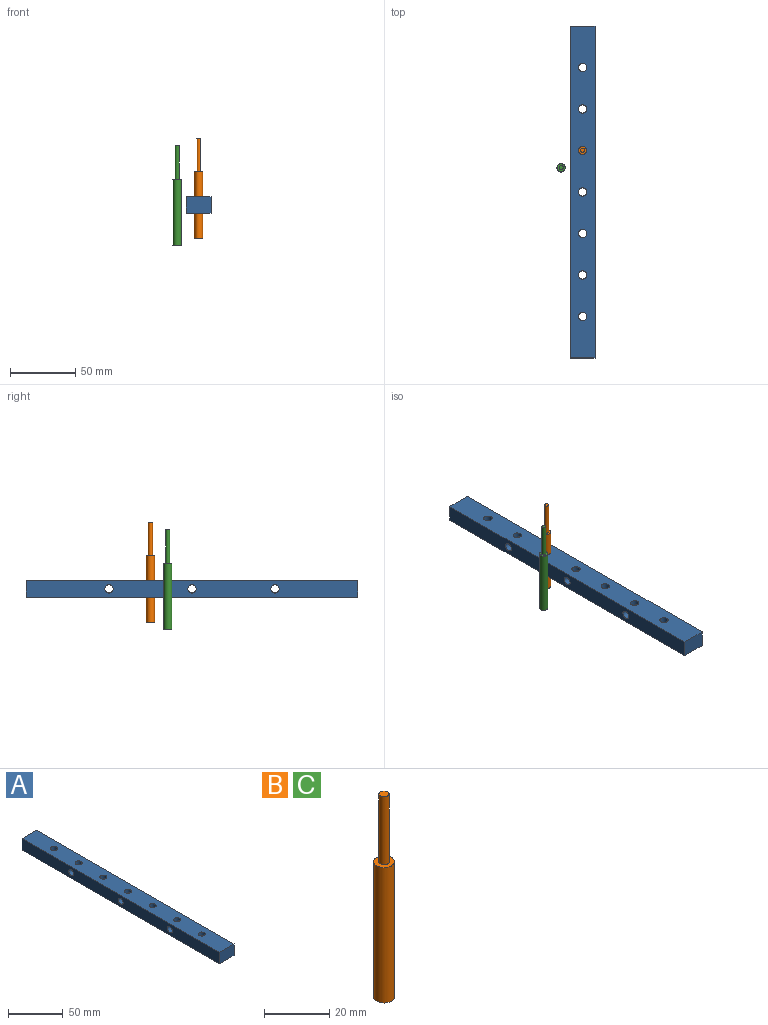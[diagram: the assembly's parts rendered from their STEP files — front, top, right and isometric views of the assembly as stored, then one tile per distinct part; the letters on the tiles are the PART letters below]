
ASSEMBLY  parts=3 mates=1
PART A: 22 faces, bbox 19.1x254x12.7 mm
  f0: cylinder r=3.17mm len=9.53mm, axis (-1,0,0), area 149.7mm2, adj f5,f16,f17
  f1: cylinder r=3.17mm len=9.53mm, axis (-1,0,0), area 149.7mm2, adj f5,f14,f15
  f2: cylinder r=3.17mm len=9.53mm, axis (-1,0,0), area 149.7mm2, adj f5,f12,f13
  f3: plane 254x12.7mm, normal (1,0,0), area 3130.8mm2, adj f4,f6,f7,f8,f9,f10,f11
  f4: plane 254x19.05mm, normal (0,0,1), area 4617mm2, adj f3,f5,f7,f8,f13,f15,f17,f18
  f5: plane 254x12.7mm, normal (-1,0,0), area 3130.8mm2, adj f0,f1,f2,f4,f6,f7,f8
  f6: plane 254x19.05mm, normal (0,0,-1), area 4617mm2, adj f3,f5,f7,f8,f12,f14,f16,f18
  f7: plane 19.05x12.7mm, normal (0,-1,0), area 241.9mm2, adj f3,f4,f5,f6
  f8: plane 19.05x12.7mm, normal (0,1,0), area 241.9mm2, adj f3,f4,f5,f6
  f9: cylinder r=3.17mm len=9.53mm, axis (-1,0,0), area 149.7mm2, adj f3,f16,f17
  f10: cylinder r=3.17mm len=9.53mm, axis (-1,0,0), area 149.7mm2, adj f3,f14,f15
  f11: cylinder r=3.17mm len=9.53mm, axis (-1,0,0), area 149.7mm2, adj f3,f12,f13
  f12: cylinder r=3.17mm len=6.35mm, axis (0,0,-1), area 86.4mm2, adj f2,f6,f11
  f13: cylinder r=3.17mm len=6.35mm, axis (0,0,-1), area 86.4mm2, adj f2,f4,f11
  f14: cylinder r=3.17mm len=6.35mm, axis (0,0,-1), area 86.4mm2, adj f1,f6,f10
  f15: cylinder r=3.17mm len=6.35mm, axis (0,0,-1), area 86.4mm2, adj f1,f4,f10
  f16: cylinder r=3.17mm len=6.35mm, axis (0,0,-1), area 86.4mm2, adj f0,f6,f9
  f17: cylinder r=3.17mm len=6.35mm, axis (0,0,-1), area 86.4mm2, adj f0,f4,f9
  f18: cylinder r=3.17mm len=12.7mm, axis (0,0,-1), area 253.4mm2, adj f4,f6
  f19: cylinder r=3.17mm len=12.7mm, axis (0,0,-1), area 253.4mm2, adj f4,f6
  f20: cylinder r=3.17mm len=12.7mm, axis (0,0,-1), area 253.4mm2, adj f4,f6
  f21: cylinder r=3.17mm len=12.7mm, axis (0,0,-1), area 253.4mm2, adj f4,f6
PART B: 5 faces, bbox 6.4x6.4x76.2 mm
  f0: cylinder r=3.17mm len=50.8mm, axis (0,0,-1), area 1013.4mm2, adj f1,f3
  f1: plane 6.35x6.35mm, normal (0,0,-1), area 31.7mm2, adj f0
  f2: cylinder r=1.59mm len=25.4mm, axis (0,0,1), area 253.4mm2, adj f3,f4
  f3: plane 6.35x6.35mm, normal (0,0,1), area 23.8mm2, adj f0,f2
  f4: plane 3.18x3.18mm, normal (0,0,1), area 7.9mm2, adj f2
PART C: same geometry as B
PLACE A t=(-150.88,1.01,-23.39)mm
PLACE B t=(-150.88,-94.24,-48.79)mm
PLACE C t=(-167.3,-107.49,-54.45)mm
MATE fastened A.f19 <-> B.f0  axis (0,0,-1) through (-150.88,-94.24,-23.39)mm
